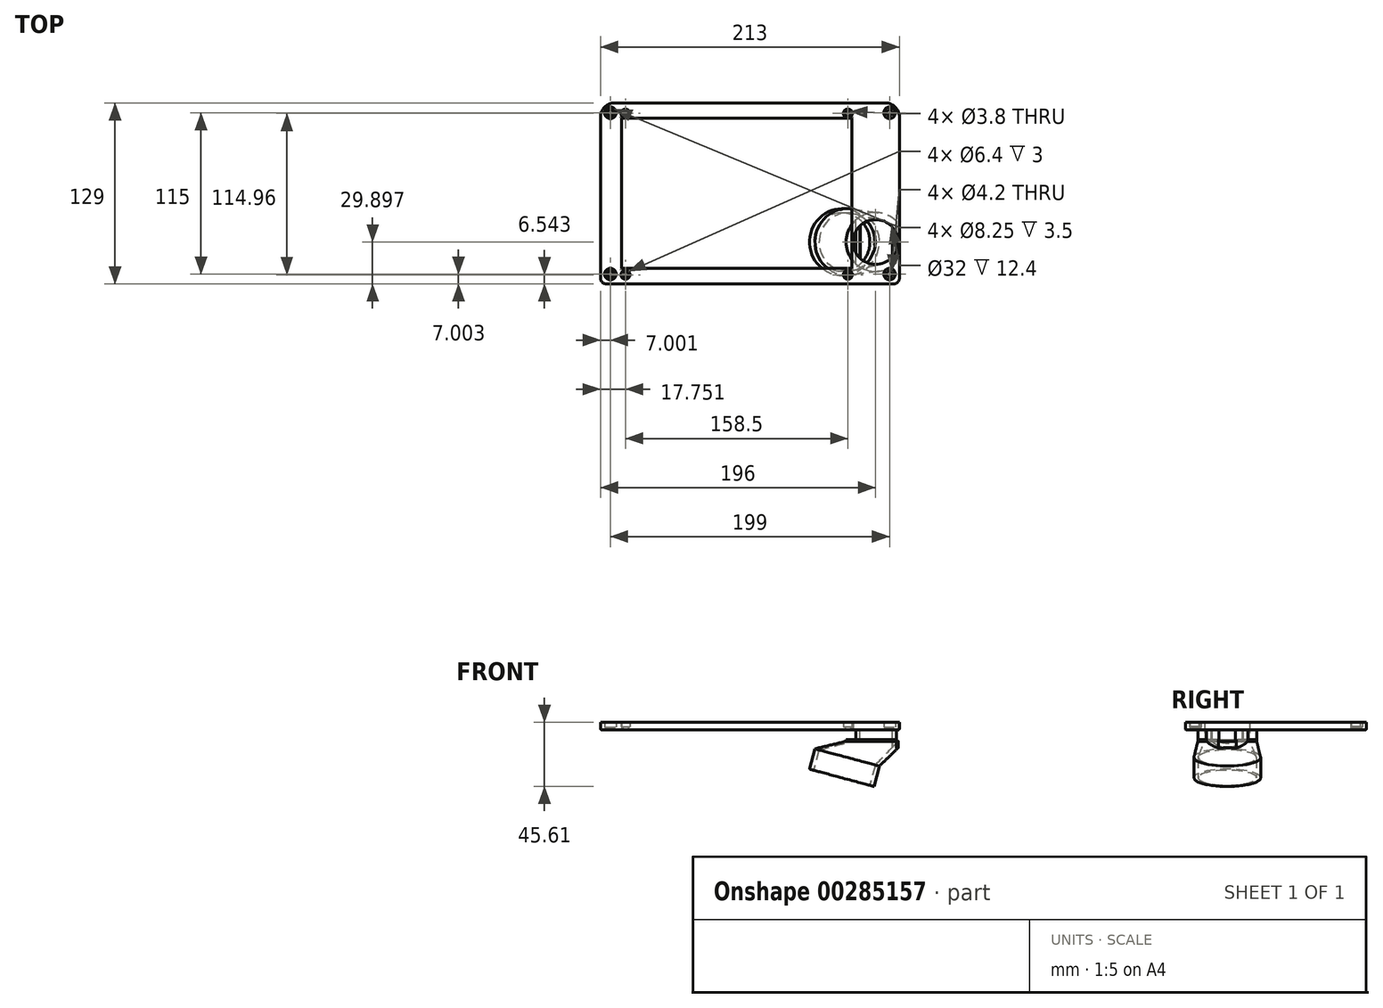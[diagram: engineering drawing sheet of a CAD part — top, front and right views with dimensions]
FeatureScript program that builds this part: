
annotation { "Feature Type Name" : "Feature", "Feature Type Description" : "" }
export const myFeature = defineFeature(function(context is Context, id is Id, definition is map)
    precondition{}
    {
        {
            var Q0;
            Q0=qCreatedBy(makeId("Top.planeOp"),FACE);
            var sketch = newSketch(context, id + "F0", { "sketchPlane" : qUnion([Q0])});
            skLineSegment(sketch, "E0.bottom", {"start": v(-110.3, 61) * mm, "end": v(82.7, 61) * mm});
            skLineSegment(sketch, "E0.top", {"start": v(-116.3, -68) * mm, "end": v(88.7, -68) * mm});
            skLineSegment(sketch, "E0.left", {"start": v(-120.3, 51) * mm, "end": v(-120.3, -64) * mm});
            skLineSegment(sketch, "E0.right", {"start": v(92.7, 51) * mm, "end": v(92.7, -64) * mm});
            skPoint(sketch, "E0.middle", {"position": v(-13.8, -3.5) * mm});
            skPoint(sketch, "E1.visualSharp", {"position": v(92.7, 61) * mm});
            skArc(sketch, "E1.filletArc", {"start": v(92.7, 51) * mm, "mid": v(89.76, 58.06) * mm, "end": v(82.7, 61) * mm});
            skPoint(sketch, "E2.visualSharp", {"position": v(-120.3, 61) * mm});
            skArc(sketch, "E2.filletArc", {"start": v(-110.3, 61) * mm, "mid": v(-117.38, 58.06) * mm, "end": v(-120.3, 51) * mm});
            skPoint(sketch, "E3.visualSharp", {"position": v(-120.3, -68) * mm});
            skArc(sketch, "E3.filletArc", {"start": v(-120.3, -64) * mm, "mid": v(-119.14, -66.84) * mm, "end": v(-116.3, -68) * mm});
            skPoint(sketch, "E4.visualSharp", {"position": v(92.7, -68) * mm});
            skArc(sketch, "E4.filletArc", {"start": v(88.7, -68) * mm, "mid": v(91.52, -66.84) * mm, "end": v(92.7, -64) * mm});
            skLineSegment(sketch, "E5", {"start": v(-23.3, -3.5) * mm, "end": v(-13.8, -3.5) * mm, "construction": true});
            skPoint(sketch, "E6", {"position": v(-23.3, -3.5) * mm});
            skLineSegment(sketch, "E7.bottom", {"start": v(-105.3, -57) * mm, "end": v(58.7, -57) * mm});
            skLineSegment(sketch, "E7.top", {"start": v(-105.3, 50) * mm, "end": v(58.7, 50) * mm});
            skLineSegment(sketch, "E7.left", {"start": v(-105.3, -57) * mm, "end": v(-105.3, 50) * mm});
            skLineSegment(sketch, "E7.right", {"start": v(58.7, -57) * mm, "end": v(58.7, 50) * mm});
            skLineSegment(sketch, "E8", {"start": v(92.7, 0) * mm, "end": v(58.7, 0) * mm, "construction": true});
            skLineSegment(sketch, "E9", {"start": v(75.7, 0) * mm, "end": v(75.7, 61) * mm, "construction": true});
            skLineSegment(sketch, "E10", {"start": v(75.7, 61) * mm, "end": v(75.7, -68) * mm, "construction": true});
            skCircle(sketch, "E11", {"center": v(75.7, -38.11) * mm, "radius": 16 * mm});
            skLineSegment(sketch, "E12", {"start": v(-23.3, -57) * mm, "end": v(-23.3, 61) * mm, "construction": true});
            skPoint(sketch, "E12.endSnap0", {"position": v(-23.3, 50) * mm});
            skLineSegment(sketch, "E13", {"start": v(-23.3, 61) * mm, "end": v(-23.3, -68) * mm, "construction": true});
            skLineSegment(sketch, "E14", {"start": v(-23.3, -3.5) * mm, "end": v(-101.76, -3.5) * mm, "construction": true});
            skLineSegment(sketch, "E15", {"start": v(-102.56, 50) * mm, "end": v(-102.56, 53.5) * mm, "construction": true});
            skLineSegment(sketch, "E16", {"start": v(-102.56, 53.5) * mm, "end": v(-102.56, -61.47) * mm, "construction": true});
            skLineSegment(sketch, "E17.MirrorCS", {"start": v(55.94, 53.5) * mm, "end": v(55.94, -61.47) * mm, "construction": true});
            skPoint(sketch, "E18", {"position": v(-102.56, 53.5) * mm});
            skPoint(sketch, "E19", {"position": v(55.94, 53.5) * mm});
            skPoint(sketch, "E20", {"position": v(55.94, -61.47) * mm});
            skPoint(sketch, "E21", {"position": v(-102.56, -61.47) * mm});
            skLineSegment(sketch, "E22", {"start": v(55.94, -61.47) * mm, "end": v(92.7, -61.47) * mm, "construction": true});
            skSolve(sketch);
        }
        {
            var Q0;
            Q0=makeQuery(id+"F0.imprint","IMPRINT",FACE,{"disambiguationData":[TD([[makeQuery(id+"F0.imprint","IMPRINT",EDGE,{"derivedFrom":sQuery(id+"F0.wireOp",EDGE,"E0.bottom")}),-1.0]])]});
            extrude(context, id + "F1", {"entities" : qUnion([Q0]), "depth" : 5.4 * mm});
        }
        {
            var Q0;
            Q0=makeQuery(id+"F1.opExtrude","CAP_FACE",FACE,{"disambiguationData":[OSD([sQuery(id+"F0.wireOp",EDGE,"E0.bottom"),sQuery(id+"F0.wireOp",EDGE,"E0.top"),sQuery(id+"F0.wireOp",EDGE,"E0.left"),sQuery(id+"F0.wireOp",EDGE,"E0.right"),sQuery(id+"F0.wireOp",EDGE,"E1.filletArc"),sQuery(id+"F0.wireOp",EDGE,"E2.filletArc"),sQuery(id+"F0.wireOp",EDGE,"E3.filletArc"),sQuery(id+"F0.wireOp",EDGE,"E4.filletArc"),sQuery(id+"F0.wireOp",EDGE,"E7.bottom"),sQuery(id+"F0.wireOp",EDGE,"E7.top"),sQuery(id+"F0.wireOp",EDGE,"E7.left"),sQuery(id+"F0.wireOp",EDGE,"E7.right"),sQuery(id+"F0.wireOp",EDGE,"E11")])],"isStart":true});
            var sketch = newSketch(context, id + "F2", { "sketchPlane" : qUnion([Q0])});
            skPoint(sketch, "E23.0", {"position": v(-102.56, 61.47) * mm});
            skPoint(sketch, "E24.0", {"position": v(55.94, 61.47) * mm});
            skPoint(sketch, "E25.0", {"position": v(-102.56, -53.5) * mm});
            skPoint(sketch, "E26.0", {"position": v(55.94, -53.5) * mm});
            skCircle(sketch, "E27", {"center": v(75.7, 38.11) * mm, "radius": 21 * mm});
            skCircle(sketch, "E28", {"center": v(75.7, 38.11) * mm, "radius": 24.25 * mm});
            skLineSegment(sketch, "E29.0", {"start": v(58.7, 57) * mm, "end": v(58.7, -50) * mm});
            skLineSegment(sketch, "E30.0", {"start": v(92.7, -51) * mm, "end": v(92.7, 64) * mm});
            skSolve(sketch);
        }
        {
            var Q0;
            Q0=makeQuery(id+"F1.opExtrude","CAP_FACE",FACE,{"disambiguationData":[OSD([sQuery(id+"F0.wireOp",EDGE,"E0.bottom"),sQuery(id+"F0.wireOp",EDGE,"E0.top"),sQuery(id+"F0.wireOp",EDGE,"E0.left"),sQuery(id+"F0.wireOp",EDGE,"E0.right"),sQuery(id+"F0.wireOp",EDGE,"E1.filletArc"),sQuery(id+"F0.wireOp",EDGE,"E2.filletArc"),sQuery(id+"F0.wireOp",EDGE,"E3.filletArc"),sQuery(id+"F0.wireOp",EDGE,"E4.filletArc"),sQuery(id+"F0.wireOp",EDGE,"E7.bottom"),sQuery(id+"F0.wireOp",EDGE,"E7.top"),sQuery(id+"F0.wireOp",EDGE,"E7.left"),sQuery(id+"F0.wireOp",EDGE,"E7.right"),sQuery(id+"F0.wireOp",EDGE,"E11")])],"isStart":false});
            var sketch = newSketch(context, id + "F3", { "sketchPlane" : qUnion([Q0])});
            skPoint(sketch, "E31.0", {"position": v(-102.56, 53.5) * mm});
            skPoint(sketch, "E32.0", {"position": v(55.94, 53.5) * mm});
            skPoint(sketch, "E33.0", {"position": v(55.94, -61.47) * mm});
            skPoint(sketch, "E34.0", {"position": v(-102.56, -61.47) * mm});
            skArc(sketch, "E35.0.0", {"start": v(-120.3, -64) * mm, "mid": v(-119.14, -66.84) * mm, "end": v(-116.3, -68) * mm});
            skLineSegment(sketch, "E35.0.1", {"start": v(-116.3, -68) * mm, "end": v(88.7, -68) * mm});
            skArc(sketch, "E35.0.2", {"start": v(88.7, -68) * mm, "mid": v(91.52, -66.84) * mm, "end": v(92.7, -64) * mm});
            skLineSegment(sketch, "E35.0.3", {"start": v(92.7, -64) * mm, "end": v(92.7, 51) * mm});
            skArc(sketch, "E35.0.4", {"start": v(92.7, 51) * mm, "mid": v(89.76, 58.06) * mm, "end": v(82.7, 61) * mm});
            skLineSegment(sketch, "E35.0.5", {"start": v(82.7, 61) * mm, "end": v(-110.3, 61) * mm});
            skArc(sketch, "E35.0.6", {"start": v(-110.3, 61) * mm, "mid": v(-117.38, 58.06) * mm, "end": v(-120.3, 51) * mm});
            skLineSegment(sketch, "E35.0.7", {"start": v(-120.3, 51) * mm, "end": v(-120.3, -64) * mm});
            skLineSegment(sketch, "E36", {"start": v(92.7, -61) * mm, "end": v(85.7, -61) * mm, "construction": true});
            skLineSegment(sketch, "E37", {"start": v(85.7, -61) * mm, "end": v(85.7, -68) * mm, "construction": true});
            skLineSegment(sketch, "E38", {"start": v(-113.3, -68) * mm, "end": v(-113.3, -61) * mm, "construction": true});
            skLineSegment(sketch, "E39", {"start": v(-113.3, -61) * mm, "end": v(-120.3, -61) * mm, "construction": true});
            skPoint(sketch, "E40", {"position": v(85.7, -61) * mm});
            skPoint(sketch, "E41", {"position": v(-113.3, -61) * mm});
            skLineSegment(sketch, "E42", {"start": v(85.7, 61) * mm, "end": v(85.7, 54) * mm, "construction": true});
            skLineSegment(sketch, "E43", {"start": v(-113.3, 61) * mm, "end": v(-113.3, 54) * mm, "construction": true});
            skLineSegment(sketch, "E44", {"start": v(-110.3, 61) * mm, "end": v(-125.94, 61) * mm, "construction": true});
            skLineSegment(sketch, "E45", {"start": v(-120.3, 51) * mm, "end": v(-120.3, 61) * mm, "construction": true});
            skLineSegment(sketch, "E46", {"start": v(-120.3, 54) * mm, "end": v(-113.3, 54) * mm, "construction": true});
            skLineSegment(sketch, "E47", {"start": v(82.7, 61) * mm, "end": v(120.1, 61) * mm, "construction": true});
            skLineSegment(sketch, "E48", {"start": v(92.7, 51) * mm, "end": v(92.7, 61) * mm, "construction": true});
            skLineSegment(sketch, "E49", {"start": v(92.7, 54) * mm, "end": v(85.7, 54) * mm, "construction": true});
            skPoint(sketch, "E50", {"position": v(-113.3, 54) * mm});
            skPoint(sketch, "E51", {"position": v(85.7, 54) * mm});
            skLineSegment(sketch, "E52", {"start": v(-113.3, 54) * mm, "end": v(-117.38, 58.06) * mm, "construction": true});
            skLineSegment(sketch, "E53", {"start": v(-119.14, -66.84) * mm, "end": v(-113.3, -61) * mm});
            skSolve(sketch);
        }
        {
            var Q0;
            Q0=sQuery(id+"F3.wireOp",VERTEX,"E34.0");
            var Q1;
            Q1=sQuery(id+"F3.wireOp",VERTEX,"E33.0");
            var Q2;
            Q2=sQuery(id+"F3.wireOp",VERTEX,"E32.0");
            var Q3;
            Q3=sQuery(id+"F3.wireOp",VERTEX,"E31.0");
            var Q4;
            Q4=makeQuery(id+"F1.opExtrude","SWEPT_BODY",BODY,{"disambiguationData":[OSD([sQuery(id+"F0.wireOp",EDGE,"E0.bottom"),sQuery(id+"F0.wireOp",EDGE,"E0.top"),sQuery(id+"F0.wireOp",EDGE,"E0.left"),sQuery(id+"F0.wireOp",EDGE,"E0.right"),sQuery(id+"F0.wireOp",EDGE,"E1.filletArc"),sQuery(id+"F0.wireOp",EDGE,"E2.filletArc"),sQuery(id+"F0.wireOp",EDGE,"E3.filletArc"),sQuery(id+"F0.wireOp",EDGE,"E4.filletArc"),sQuery(id+"F0.wireOp",EDGE,"E7.bottom"),sQuery(id+"F0.wireOp",EDGE,"E7.top"),sQuery(id+"F0.wireOp",EDGE,"E7.left"),sQuery(id+"F0.wireOp",EDGE,"E7.right"),sQuery(id+"F0.wireOp",EDGE,"E11")])]});
            hole(context, id + "F4", {"style" : HoleStyle.C_BORE, "endStyle" : HoleEndStyle.THROUGH, "holeDiameter" : 3.8 * mm, "cBoreDiameter" : 6.4 * mm, "cBoreDepth" : 3 * mm, "tappedDepth" : 12 * mm, "tapClearance" : 3, "locations" : qUnion([Q0, Q1, Q2, Q3]), "scope" : qUnion([Q4]), "startStyle" : HoleStartStyle.PART});
        }
        {
            var Q0;
            Q0=sQuery(id+"F3.wireOp",VERTEX,"E41");
            var Q1;
            Q1=sQuery(id+"F3.wireOp",VERTEX,"E50");
            var Q2;
            Q2=sQuery(id+"F3.wireOp",VERTEX,"E51");
            var Q3;
            Q3=sQuery(id+"F3.wireOp",VERTEX,"E40");
            var Q4;
            Q4=makeQuery(id+"F1.opExtrude","SWEPT_BODY",BODY,{"disambiguationData":[OSD([sQuery(id+"F0.wireOp",EDGE,"E0.bottom"),sQuery(id+"F0.wireOp",EDGE,"E0.top"),sQuery(id+"F0.wireOp",EDGE,"E0.left"),sQuery(id+"F0.wireOp",EDGE,"E0.right"),sQuery(id+"F0.wireOp",EDGE,"E1.filletArc"),sQuery(id+"F0.wireOp",EDGE,"E2.filletArc"),sQuery(id+"F0.wireOp",EDGE,"E3.filletArc"),sQuery(id+"F0.wireOp",EDGE,"E4.filletArc"),sQuery(id+"F0.wireOp",EDGE,"E7.bottom"),sQuery(id+"F0.wireOp",EDGE,"E7.top"),sQuery(id+"F0.wireOp",EDGE,"E7.left"),sQuery(id+"F0.wireOp",EDGE,"E7.right"),sQuery(id+"F0.wireOp",EDGE,"E11")])]});
            hole(context, id + "F5", {"style" : HoleStyle.C_BORE, "endStyle" : HoleEndStyle.THROUGH, "holeDiameter" : 4.2 * mm, "cBoreDiameter" : 8.25 * mm, "cBoreDepth" : 3.5 * mm, "tappedDepth" : 12 * mm, "tapClearance" : 3, "locations" : qUnion([Q0, Q1, Q2, Q3]), "scope" : qUnion([Q4]), "startStyle" : HoleStartStyle.PART});
        }
        {
            var Q0;
            {var subQ0=sQuery(id+"F0.wireOp",EDGE,"E7.right");var subQ1=sQuery(id+"F0.wireOp",EDGE,"E0.right");var subQ2=sQuery(id+"F2.wireOp",EDGE,"E28");Q0=makeQuery(id+"FXzu7cfs2hGkWBK_1.boolean.opBoolean","COPY",EDGE,{"disambiguationData":[TD([makeQuery(id+"F1.opExtrude","CAP_FACE",FACE,{"disambiguationData":[OSD([sQuery(id+"F0.wireOp",EDGE,"E0.bottom"),sQuery(id+"F0.wireOp",EDGE,"E0.top"),sQuery(id+"F0.wireOp",EDGE,"E0.left"),subQ1,sQuery(id+"F0.wireOp",EDGE,"E1.filletArc"),sQuery(id+"F0.wireOp",EDGE,"E2.filletArc"),sQuery(id+"F0.wireOp",EDGE,"E3.filletArc"),sQuery(id+"F0.wireOp",EDGE,"E4.filletArc"),sQuery(id+"F0.wireOp",EDGE,"E7.bottom"),sQuery(id+"F0.wireOp",EDGE,"E7.top"),sQuery(id+"F0.wireOp",EDGE,"E7.left"),subQ0,sQuery(id+"F0.wireOp",EDGE,"E11")])],"isStart":true}),makeQuery(id+"F1.opExtrude","SWEPT_FACE",FACE,{"disambiguationData":[OSD([subQ1])]}),makeQuery(id+"F1.opExtrude","SWEPT_FACE",FACE,{"disambiguationData":[OSD([subQ0])]}),makeQuery(id+"FXzu7cfs2hGkWBK_1.opExtrude","SWEPT_FACE",FACE,{"disambiguationData":[OSD([subQ2])]})])],"derivedFrom":makeQuery(id+"FXzu7cfs2hGkWBK_1.opExtrude","CAP_EDGE",EDGE,{"disambiguationData":[OSD([subQ2])],"isStart":true})});}
            var Q1;
            {var subQ0=sQuery(id+"F0.wireOp",EDGE,"E7.right");var subQ1=sQuery(id+"F2.wireOp",EDGE,"E28");Q1=makeQuery(id+"FXzu7cfs2hGkWBK_1.boolean.opBoolean","COPY",EDGE,{"disambiguationData":[TD([makeQuery(id+"F1.opExtrude","CAP_FACE",FACE,{"disambiguationData":[OSD([sQuery(id+"F0.wireOp",EDGE,"E0.bottom"),sQuery(id+"F0.wireOp",EDGE,"E0.top"),sQuery(id+"F0.wireOp",EDGE,"E0.left"),sQuery(id+"F0.wireOp",EDGE,"E0.right"),sQuery(id+"F0.wireOp",EDGE,"E1.filletArc"),sQuery(id+"F0.wireOp",EDGE,"E2.filletArc"),sQuery(id+"F0.wireOp",EDGE,"E3.filletArc"),sQuery(id+"F0.wireOp",EDGE,"E4.filletArc"),sQuery(id+"F0.wireOp",EDGE,"E7.bottom"),sQuery(id+"F0.wireOp",EDGE,"E7.top"),sQuery(id+"F0.wireOp",EDGE,"E7.left"),subQ0,sQuery(id+"F0.wireOp",EDGE,"E11")])],"isStart":true}),makeQuery(id+"F1.opExtrude","SWEPT_FACE",FACE,{"disambiguationData":[OSD([subQ0])]}),makeQuery(id+"F5.hole-3.boolean.opBoolean","COPY",FACE,{"derivedFrom":makeQuery(id+"F5.hole-3.opRevolve","SWEPT_FACE",FACE,{"disambiguationData":[OSD([sQuery(id+"F5.hole-3.sketch.wireOp",EDGE,"core_line_2")])]})}),makeQuery(id+"FXzu7cfs2hGkWBK_1.opExtrude","SWEPT_FACE",FACE,{"disambiguationData":[OSD([subQ1])]})])],"derivedFrom":makeQuery(id+"FXzu7cfs2hGkWBK_1.opExtrude","CAP_EDGE",EDGE,{"disambiguationData":[OSD([subQ1])],"isStart":true})});}
            var Q2;
            Q2=makeQuery(id+"F1.opExtrude","CAP_EDGE",EDGE,{"disambiguationData":[OSD([sQuery(id+"F0.wireOp",EDGE,"E0.left")])],"isStart":true});
            var Q3;
            Q3=makeQuery(id+"F1.opExtrude","CAP_EDGE",EDGE,{"disambiguationData":[OSD([sQuery(id+"F0.wireOp",EDGE,"E2.filletArc")])],"isStart":true});
            var Q4;
            Q4=makeQuery(id+"F1.opExtrude","CAP_EDGE",EDGE,{"disambiguationData":[OSD([sQuery(id+"F0.wireOp",EDGE,"E7.bottom")])],"isStart":true});
            var Q5;
            Q5=makeQuery(id+"F1.opExtrude","CAP_EDGE",EDGE,{"disambiguationData":[OSD([sQuery(id+"F0.wireOp",EDGE,"E7.left")])],"isStart":true});
            var Q6;
            Q6=makeQuery(id+"F1.opExtrude","CAP_EDGE",EDGE,{"disambiguationData":[OSD([sQuery(id+"F0.wireOp",EDGE,"E7.top")])],"isStart":true});
            var Q7;
            {var subQ0=sQuery(id+"F0.wireOp",EDGE,"E7.right");var subQ1=sQuery(id+"F0.wireOp",EDGE,"E7.bottom");Q7=makeQuery(id+"FXzu7cfs2hGkWBK_1.boolean.opBoolean","SPLIT",EDGE,{"disambiguationData":[TD([makeQuery(id+"F1.opExtrude","SWEPT_FACE",FACE,{"disambiguationData":[OSD([subQ1])]})])],"derivedFrom":makeQuery(id+"F1.opExtrude","CAP_EDGE",EDGE,{"disambiguationData":[OSD([subQ0])],"isStart":true})});}
            var Q8;
            {var subQ0=sQuery(id+"F0.wireOp",EDGE,"E7.right");Q8=makeQuery(id+"FXzu7cfs2hGkWBK_1.boolean.opBoolean","SPLIT",EDGE,{"disambiguationData":[TD([makeQuery(id+"FXzu7cfs2hGkWBK_1.opExtrude","SWEPT_FACE",FACE,{"disambiguationData":[OSD([sQuery(id+"F2.wireOp",EDGE,"E27")])]})])],"derivedFrom":makeQuery(id+"F1.opExtrude","CAP_EDGE",EDGE,{"disambiguationData":[OSD([subQ0])],"isStart":true})});}
            var Q9;
            {var subQ0=sQuery(id+"F0.wireOp",EDGE,"E7.right");var subQ1=sQuery(id+"F0.wireOp",EDGE,"E7.top");var subQ3=makeQuery(id+"F1.opExtrude","SWEPT_FACE",FACE,{"disambiguationData":[OSD([subQ1])]});Q9=makeQuery(id+"FAuTDVlshv62hnW_1.boolean.opBoolean","SPLIT",EDGE,{"disambiguationData":[TD([subQ3])],"derivedFrom":makeQuery(id+"FXzu7cfs2hGkWBK_1.boolean.opBoolean","SPLIT",EDGE,{"disambiguationData":[TD([subQ3])],"derivedFrom":makeQuery(id+"F1.opExtrude","CAP_EDGE",EDGE,{"disambiguationData":[OSD([subQ0])],"isStart":true})})});}
            var Q10;
            {var subQ0=sQuery(id+"F0.wireOp",EDGE,"E7.right");var subQ1=sQuery(id+"F0.wireOp",EDGE,"E7.top");var subQ2=sQuery(id+"F0.wireOp",EDGE,"E0.right");var subQ3=makeQuery(id+"F1.opExtrude","CAP_FACE",FACE,{"disambiguationData":[OSD([sQuery(id+"F0.wireOp",EDGE,"E0.bottom"),sQuery(id+"F0.wireOp",EDGE,"E0.top"),sQuery(id+"F0.wireOp",EDGE,"E0.left"),subQ2,sQuery(id+"F0.wireOp",EDGE,"E1.filletArc"),sQuery(id+"F0.wireOp",EDGE,"E2.filletArc"),sQuery(id+"F0.wireOp",EDGE,"E3.filletArc"),sQuery(id+"F0.wireOp",EDGE,"E4.filletArc"),sQuery(id+"F0.wireOp",EDGE,"E7.bottom"),subQ1,sQuery(id+"F0.wireOp",EDGE,"E7.left"),subQ0,sQuery(id+"F0.wireOp",EDGE,"E11")])],"isStart":true});var subQ4=makeQuery(id+"F1.opExtrude","SWEPT_FACE",FACE,{"disambiguationData":[OSD([subQ0])]});var subQ5=sQuery(id+"F2.wireOp",EDGE,"E28");var subQ6=makeQuery(id+"FXzu7cfs2hGkWBK_1.opExtrude","SWEPT_FACE",FACE,{"disambiguationData":[OSD([subQ5])]});Q10=makeQuery(id+"FAuTDVlshv62hnW_1.boolean.opBoolean","SPLIT",EDGE,{"disambiguationData":[TD([makeQuery(id+"FXzu7cfs2hGkWBK_1.boolean.opBoolean","COPY",FACE,{"disambiguationData":[TD([subQ3,makeQuery(id+"F1.opExtrude","SWEPT_FACE",FACE,{"disambiguationData":[OSD([subQ2])]}),subQ4,makeQuery(id+"FXzu7cfs2hGkWBK_1.opExtrude","CAP_FACE",FACE,{"disambiguationData":[OSD([sQuery(id+"F2.wireOp",EDGE,"E27"),subQ5])],"isStart":false})])],"derivedFrom":subQ6})])],"derivedFrom":makeQuery(id+"FXzu7cfs2hGkWBK_1.boolean.opBoolean","SPLIT",EDGE,{"disambiguationData":[TD([makeQuery(id+"F1.opExtrude","SWEPT_FACE",FACE,{"disambiguationData":[OSD([subQ1])]})])],"derivedFrom":makeQuery(id+"F1.opExtrude","CAP_EDGE",EDGE,{"disambiguationData":[OSD([subQ0])],"isStart":true})})});}
            var Q11;
            {var subQ0=sQuery(id+"F0.wireOp",EDGE,"E7.right");var subQ1=sQuery(id+"F0.wireOp",EDGE,"E7.top");Q11=makeQuery(id+"FAuTDVlshv62hnW_1.boolean.opBoolean","SPLIT",EDGE,{"disambiguationData":[TD([makeQuery(id+"FAuTDVlshv62hnW_1.opExtrude","SWEPT_FACE",FACE,{"disambiguationData":[OSD([sQuery(id+"F2.wireOp",EDGE,"AH5NIqyg-kwf5-ivtZ-E1gb-oLSIGUMr4FpD")])]})])],"derivedFrom":makeQuery(id+"FXzu7cfs2hGkWBK_1.boolean.opBoolean","SPLIT",EDGE,{"disambiguationData":[TD([makeQuery(id+"F1.opExtrude","SWEPT_FACE",FACE,{"disambiguationData":[OSD([subQ1])]})])],"derivedFrom":makeQuery(id+"F1.opExtrude","CAP_EDGE",EDGE,{"disambiguationData":[OSD([subQ0])],"isStart":true})})});}
            var Q12;
            Q12=makeQuery(id+"FAuTDVlshv62hnW_1.boolean.opBoolean","COPY",EDGE,{"disambiguationData":[OD(0.0)],"derivedFrom":makeQuery(id+"FAuTDVlshv62hnW_1.opExtrude","CAP_EDGE",EDGE,{"disambiguationData":[OSD([sQuery(id+"F2.wireOp",EDGE,"opVQtyLN-j1gY-ZvLt-gBJu-Jvu7VNzgkRLF")])],"isStart":true})});
            var Q13;
            Q13=makeQuery(id+"FAuTDVlshv62hnW_1.boolean.opBoolean","COPY",EDGE,{"disambiguationData":[OD(1.0)],"derivedFrom":makeQuery(id+"FAuTDVlshv62hnW_1.opExtrude","CAP_EDGE",EDGE,{"disambiguationData":[OSD([sQuery(id+"F2.wireOp",EDGE,"opVQtyLN-j1gY-ZvLt-gBJu-Jvu7VNzgkRLF")])],"isStart":true})});
            var Q14;
            Q14=makeQuery(id+"F1.opExtrude","CAP_EDGE",EDGE,{"disambiguationData":[OSD([sQuery(id+"F0.wireOp",EDGE,"E0.bottom")])],"isStart":true});
            var Q15;
            Q15=makeQuery(id+"F1.opExtrude","CAP_EDGE",EDGE,{"disambiguationData":[OSD([sQuery(id+"F0.wireOp",EDGE,"E1.filletArc")])],"isStart":true});
            var Q16;
            {var subQ0=sQuery(id+"F0.wireOp",EDGE,"E0.right");Q16=makeQuery(id+"FXzu7cfs2hGkWBK_1.boolean.opBoolean","SPLIT",EDGE,{"disambiguationData":[TD([makeQuery(id+"FXzu7cfs2hGkWBK_1.opExtrude","SWEPT_FACE",FACE,{"disambiguationData":[OSD([sQuery(id+"F2.wireOp",EDGE,"E27")])]})])],"derivedFrom":makeQuery(id+"F1.opExtrude","CAP_EDGE",EDGE,{"disambiguationData":[OSD([subQ0])],"isStart":true})});}
            var Q17;
            {var subQ0=sQuery(id+"F0.wireOp",EDGE,"E1.filletArc");var subQ1=sQuery(id+"F0.wireOp",EDGE,"E0.right");var subQ3=makeQuery(id+"F1.opExtrude","SWEPT_FACE",FACE,{"disambiguationData":[OSD([subQ0])]});Q17=makeQuery(id+"FAuTDVlshv62hnW_1.boolean.opBoolean","SPLIT",EDGE,{"disambiguationData":[TD([subQ3])],"derivedFrom":makeQuery(id+"FXzu7cfs2hGkWBK_1.boolean.opBoolean","SPLIT",EDGE,{"disambiguationData":[TD([subQ3])],"derivedFrom":makeQuery(id+"F1.opExtrude","CAP_EDGE",EDGE,{"disambiguationData":[OSD([subQ1])],"isStart":true})})});}
            var Q18;
            {var subQ0=sQuery(id+"F0.wireOp",EDGE,"E7.right");var subQ1=sQuery(id+"F0.wireOp",EDGE,"E1.filletArc");var subQ2=sQuery(id+"F0.wireOp",EDGE,"E0.right");var subQ3=makeQuery(id+"F1.opExtrude","CAP_FACE",FACE,{"disambiguationData":[OSD([sQuery(id+"F0.wireOp",EDGE,"E0.bottom"),sQuery(id+"F0.wireOp",EDGE,"E0.top"),sQuery(id+"F0.wireOp",EDGE,"E0.left"),subQ2,subQ1,sQuery(id+"F0.wireOp",EDGE,"E2.filletArc"),sQuery(id+"F0.wireOp",EDGE,"E3.filletArc"),sQuery(id+"F0.wireOp",EDGE,"E4.filletArc"),sQuery(id+"F0.wireOp",EDGE,"E7.bottom"),sQuery(id+"F0.wireOp",EDGE,"E7.top"),sQuery(id+"F0.wireOp",EDGE,"E7.left"),subQ0,sQuery(id+"F0.wireOp",EDGE,"E11")])],"isStart":true});var subQ4=makeQuery(id+"F1.opExtrude","SWEPT_FACE",FACE,{"disambiguationData":[OSD([subQ2])]});var subQ5=sQuery(id+"F2.wireOp",EDGE,"E28");var subQ6=makeQuery(id+"FXzu7cfs2hGkWBK_1.opExtrude","SWEPT_FACE",FACE,{"disambiguationData":[OSD([subQ5])]});Q18=makeQuery(id+"FAuTDVlshv62hnW_1.boolean.opBoolean","SPLIT",EDGE,{"disambiguationData":[TD([makeQuery(id+"FXzu7cfs2hGkWBK_1.boolean.opBoolean","COPY",FACE,{"disambiguationData":[TD([subQ3,subQ4,makeQuery(id+"F1.opExtrude","SWEPT_FACE",FACE,{"disambiguationData":[OSD([subQ0])]}),makeQuery(id+"FXzu7cfs2hGkWBK_1.opExtrude","CAP_FACE",FACE,{"disambiguationData":[OSD([sQuery(id+"F2.wireOp",EDGE,"E27"),subQ5])],"isStart":false})])],"derivedFrom":subQ6})])],"derivedFrom":makeQuery(id+"FXzu7cfs2hGkWBK_1.boolean.opBoolean","SPLIT",EDGE,{"disambiguationData":[TD([makeQuery(id+"F1.opExtrude","SWEPT_FACE",FACE,{"disambiguationData":[OSD([subQ1])]})])],"derivedFrom":makeQuery(id+"F1.opExtrude","CAP_EDGE",EDGE,{"disambiguationData":[OSD([subQ2])],"isStart":true})})});}
            var Q19;
            {var subQ0=sQuery(id+"F0.wireOp",EDGE,"E1.filletArc");var subQ1=sQuery(id+"F0.wireOp",EDGE,"E0.right");Q19=makeQuery(id+"FAuTDVlshv62hnW_1.boolean.opBoolean","SPLIT",EDGE,{"disambiguationData":[TD([makeQuery(id+"FAuTDVlshv62hnW_1.opExtrude","SWEPT_FACE",FACE,{"disambiguationData":[OSD([sQuery(id+"F2.wireOp",EDGE,"AH5NIqyg-kwf5-ivtZ-E1gb-oLSIGUMr4FpD")])]})])],"derivedFrom":makeQuery(id+"FXzu7cfs2hGkWBK_1.boolean.opBoolean","SPLIT",EDGE,{"disambiguationData":[TD([makeQuery(id+"F1.opExtrude","SWEPT_FACE",FACE,{"disambiguationData":[OSD([subQ0])]})])],"derivedFrom":makeQuery(id+"F1.opExtrude","CAP_EDGE",EDGE,{"disambiguationData":[OSD([subQ1])],"isStart":true})})});}
            var Q20;
            Q20=makeQuery(id+"F1.opExtrude","CAP_EDGE",EDGE,{"disambiguationData":[OSD([sQuery(id+"F0.wireOp",EDGE,"E4.filletArc")])],"isStart":true});
            var Q21;
            Q21=makeQuery(id+"F1.opExtrude","CAP_EDGE",EDGE,{"disambiguationData":[OSD([sQuery(id+"F0.wireOp",EDGE,"E3.filletArc")])],"isStart":true});
            var Q22;
            Q22=makeQuery(id+"FAuTDVlshv62hnW_1.boolean.opBoolean","COPY",EDGE,{"disambiguationData":[OD(0.0)],"derivedFrom":makeQuery(id+"FAuTDVlshv62hnW_1.opExtrude","CAP_EDGE",EDGE,{"disambiguationData":[OSD([sQuery(id+"F2.wireOp",EDGE,"AH5NIqyg-kwf5-ivtZ-E1gb-oLSIGUMr4FpD")])],"isStart":true})});
            var Q23;
            Q23=makeQuery(id+"FAuTDVlshv62hnW_1.boolean.opBoolean","COPY",EDGE,{"disambiguationData":[OD(1.0)],"derivedFrom":makeQuery(id+"FAuTDVlshv62hnW_1.opExtrude","CAP_EDGE",EDGE,{"disambiguationData":[OSD([sQuery(id+"F2.wireOp",EDGE,"AH5NIqyg-kwf5-ivtZ-E1gb-oLSIGUMr4FpD")])],"isStart":true})});
            var Q24;
            Q24=makeQuery(id+"FXzu7cfs2hGkWBK_1.boolean.opBoolean","COPY",EDGE,{"disambiguationData":[OD(0.0)],"derivedFrom":makeQuery(id+"FXzu7cfs2hGkWBK_1.opExtrude","CAP_EDGE",EDGE,{"disambiguationData":[OSD([sQuery(id+"F2.wireOp",EDGE,"E27")])],"isStart":true})});
            var Q25;
            Q25=makeQuery(id+"FXzu7cfs2hGkWBK_1.boolean.opBoolean","COPY",EDGE,{"disambiguationData":[OD(1.0)],"derivedFrom":makeQuery(id+"FXzu7cfs2hGkWBK_1.opExtrude","CAP_EDGE",EDGE,{"disambiguationData":[OSD([sQuery(id+"F2.wireOp",EDGE,"E27")])],"isStart":true})});
            var Q26;
            Q26=makeQuery(id+"F1.opExtrude","CAP_EDGE",EDGE,{"disambiguationData":[OSD([sQuery(id+"F0.wireOp",EDGE,"E0.top")])],"isStart":true});
            fillet(context, id + "F6", {"entities" : qUnion([Q0, Q1, Q2, Q3, Q4, Q5, Q6, Q7, Q8, Q9, Q10, Q11, Q12, Q13, Q14, Q15, Q16, Q17, Q18, Q19, Q20, Q21, Q22, Q23, Q24, Q25, Q26]), "radius" : 1 * mm, "tangentPropagation" : true, "allowEdgeOverflow" : false});
        }
        {
            var Q0;
            Q0=makeQuery(id+"F2.imprint","IMPRINT",FACE,{"disambiguationData":[TD([[makeQuery(id+"F2.imprint","IMPRINT",EDGE,{"derivedFrom":makeQuery(id+"F1.opExtrude","CAP_EDGE",EDGE,{"disambiguationData":[OSD([sQuery(id+"F0.wireOp",EDGE,"E11")])],"isStart":true})}),1.0]])]});
            var sketch = newSketch(context, id + "F7", { "sketchPlane" : qUnion([Q0])});
            skCircle(sketch, "E54.0", {"center": v(75.7, 38.11) * mm, "radius": 16 * mm});
            skCircle(sketch, "E55.0", {"center": v(75.7, 38.11) * mm, "radius": 21 * mm});
            skLineSegment(sketch, "E56", {"start": v(61.54, 53.63) * mm, "end": v(61.54, 22.6) * mm});
            skLineSegment(sketch, "E57", {"start": v(90.57, 52.93) * mm, "end": v(90.57, 23.3) * mm});
            skSolve(sketch);
        }
        {
            var Q0;
            Q0=makeQuery(id+"F0.imprint","IMPRINT",FACE,{"disambiguationData":[TD([[makeQuery(id+"F0.imprint","IMPRINT",EDGE,{"derivedFrom":sQuery(id+"F0.wireOp",EDGE,"E11")}),1.0]])]});
            cPlane(context, id + "F8", {"entities" : qUnion([Q0]), "cplaneType" : CPlaneType.OFFSET, "offset" : 35 * mm, "oppositeDirection" : true, "width" : 150 * mm, "height" : 150 * mm});
        }
        {
            var Q0;
            Q0=qCreatedBy(id+"F8.planeOp",FACE);
            var sketch = newSketch(context, id + "F9", { "sketchPlane" : qUnion([Q0])});
            skPoint(sketch, "E58.0", {"position": v(75.7, -38.11) * mm});
            skLineSegment(sketch, "E59", {"start": v(75.7, -38.11) * mm, "end": v(60.7, -38.11) * mm, "construction": true});
            skCircle(sketch, "E60", {"center": v(60.7, -38.11) * mm, "radius": 20.75 * mm});
            skCircle(sketch, "E61", {"center": v(60.7, -38.11) * mm, "radius": 23.75 * mm});
            skSolve(sketch);
        }
        {
            var Q0;
            Q0=makeQuery(id+"F9.imprint","IMPRINT",FACE,{"disambiguationData":[TD([[makeQuery(id+"F9.imprint","IMPRINT",EDGE,{"derivedFrom":sQuery(id+"F9.wireOp",EDGE,"E60")}),-1.0]])]});
            extrude(context, id + "F10", {"entities" : qUnion([Q0]), "operationType" : NewBodyOperationType.ADD, "depth" : 15 * mm});
        }
        {
            var Q0;
            Q0=makeQuery(id+"F10.opExtrude","SWEPT_BODY",BODY,{"disambiguationData":[OSD([sQuery(id+"F9.wireOp",EDGE,"E60"),sQuery(id+"F9.wireOp",EDGE,"E61"),sQuery(id+"F9.wireOp",EDGE,"JfIrUzmG-d9lY-iVxp-Mb9g-9npJm7Iwwub6"),sQuery(id+"F9.wireOp",EDGE,"MjCc8q1w-3G2U-IAaR-hrDx-Pos9HdKJ4R0N")])]});
            var Q1;
            Q1=makeQuery(id+"F10.opExtrude","SWEPT_BODY",BODY,{"disambiguationData":[OSD([sQuery(id+"F9.wireOp",EDGE,"E60"),sQuery(id+"F9.wireOp",EDGE,"E61"),sQuery(id+"F9.wireOp",EDGE,"8tNqm4Kz-eikn-GZsH-ny9o-i7E9EC5gfrlz"),sQuery(id+"F9.wireOp",EDGE,"Jv5iIJlW-SeG2-jAlZ-grfs-9UxCIiy8JIfF")])]});
            var Q2;
            {var subQ0=sQuery(id+"F0.wireOp",EDGE,"E7.right");Q2=makeQuery(id+"F6.opFillet","BLEND_EDGE",EDGE,{"disambiguationData":[OD(0.0)],"blendedFrom":[makeQuery(id+"F1.opExtrude","CAP_EDGE",EDGE,{"disambiguationData":[OSD([subQ0])],"isStart":true}),makeQuery(id+"F1.opExtrude","CAP_FACE",FACE,{"disambiguationData":[OSD([sQuery(id+"F0.wireOp",EDGE,"E0.bottom"),sQuery(id+"F0.wireOp",EDGE,"E0.top"),sQuery(id+"F0.wireOp",EDGE,"E0.left"),sQuery(id+"F0.wireOp",EDGE,"E0.right"),sQuery(id+"F0.wireOp",EDGE,"E1.filletArc"),sQuery(id+"F0.wireOp",EDGE,"E2.filletArc"),sQuery(id+"F0.wireOp",EDGE,"E3.filletArc"),sQuery(id+"F0.wireOp",EDGE,"E4.filletArc"),sQuery(id+"F0.wireOp",EDGE,"E7.bottom"),sQuery(id+"F0.wireOp",EDGE,"E7.top"),sQuery(id+"F0.wireOp",EDGE,"E7.left"),subQ0,sQuery(id+"F0.wireOp",EDGE,"E11")])],"isStart":true})],"blendedInto":[makeQuery(id+"F1.opExtrude","CAP_FACE",FACE,{"disambiguationData":[OSD([sQuery(id+"F0.wireOp",EDGE,"E0.bottom"),sQuery(id+"F0.wireOp",EDGE,"E0.top"),sQuery(id+"F0.wireOp",EDGE,"E0.left"),sQuery(id+"F0.wireOp",EDGE,"E0.right"),sQuery(id+"F0.wireOp",EDGE,"E1.filletArc"),sQuery(id+"F0.wireOp",EDGE,"E2.filletArc"),sQuery(id+"F0.wireOp",EDGE,"E3.filletArc"),sQuery(id+"F0.wireOp",EDGE,"E4.filletArc"),sQuery(id+"F0.wireOp",EDGE,"E7.bottom"),sQuery(id+"F0.wireOp",EDGE,"E7.top"),sQuery(id+"F0.wireOp",EDGE,"E7.left"),subQ0,sQuery(id+"F0.wireOp",EDGE,"E11")])],"isStart":true})]});}
            transform(context, id + "F11", {"entities" : qUnion([Q0, Q1]), "transformType" : TransformType.ROTATION, "transformAxis" : qUnion([Q2]), "angle" : 15 * degree, "makeCopy" : false});
        }
        {
            var Q0;
            Q0=makeQuery(id+"F7.imprint","IMPRINT",FACE,{"disambiguationData":[TD([[makeQuery(id+"F7.imprint","IMPRINT",EDGE,{"derivedFrom":sQuery(id+"F7.wireOp",EDGE,"E54.0")}),1.0]])]});
            extrude(context, id + "F12", {"entities" : qUnion([Q0]), "depth" : 7 * mm});
        }
        {
            var Q0;
            {var subQ0=sQuery(id+"F7.wireOp",EDGE,"E57");var subQ1=sQuery(id+"F7.wireOp",EDGE,"E55.0");var subQ2=makeQuery(id+"F7.imprint","INTERSECT",VERTEX,{"disambiguationData":[OD(1.0)],"derivedFrom":[subQ1,subQ0]});var subQ3=sQuery(id+"F7.wireOp",EDGE,"E54.0");var subQ5=sQuery(id+"F7.wireOp",EDGE,"E56");var subQ6=makeQuery(id+"F7.imprint","INTERSECT",VERTEX,{"disambiguationData":[OD(1.0)],"derivedFrom":[subQ1,subQ5]});var subQ7=makeQuery(id+"F7.imprint","INTERSECT",VERTEX,{"disambiguationData":[OD(0.0)],"derivedFrom":[subQ3,subQ5]});Q0=makeQuery(id+"F12.opExtrude","CAP_FACE",FACE,{"disambiguationData":[OSD([subQ3,subQ1,subQ5,subQ0]),TDD([makeQuery(id+"F7.imprint","IMPRINT",EDGE,{"disambiguationData":[TD([[subQ7,1.0]])],"derivedFrom":subQ3}),makeQuery(id+"F7.imprint","IMPRINT",EDGE,{"disambiguationData":[TD([[subQ6,-1.0]])],"derivedFrom":subQ1}),makeQuery(id+"F7.imprint","IMPRINT",EDGE,{"disambiguationData":[TD([[subQ6,1.0]])],"derivedFrom":subQ5}),makeQuery(id+"F7.imprint","IMPRINT",EDGE,{"disambiguationData":[TD([[subQ2,1.0]])],"derivedFrom":subQ0})])],"isStart":false});}
            var sketch = newSketch(context, id + "F13", { "sketchPlane" : qUnion([Q0])});
            skCircle(sketch, "E62", {"center": v(75.7, 38.11) * mm, "radius": 16.15 * mm});
            skCircle(sketch, "E63", {"center": v(75.7, 38.11) * mm, "radius": 20.97 * mm});
            skSolve(sketch);
        }
        {
            var Q0;
            Q0 = qSketchRegion(id + "F13", true);
            extrude(context, id + "F14", {"entities" : qUnion([Q0]), "operationType" : NewBodyOperationType.ADD, "depth" : 1 * mm});
        }
        {
            var Q0;
            Q0=makeQuery(id+"F14.opExtrude","CAP_FACE",FACE,{"disambiguationData":[OSD([sQuery(id+"F13.wireOp",EDGE,"E62"),sQuery(id+"F13.wireOp",EDGE,"E63")])],"isStart":false});
            var sketch = newSketch(context, id + "F15", { "sketchPlane" : qUnion([Q0])});
            skCircle(sketch, "E64.0.0", {"center": v(75.7, 38.11) * mm, "radius": 20.97 * mm});
            skCircle(sketch, "E65.0", {"center": v(75.7, 38.11) * mm, "radius": 16.15 * mm});
            skLineSegment(sketch, "E66", {"start": v(76.03, 21.96) * mm, "end": v(76.03, 17.14) * mm});
            skLineSegment(sketch, "E67", {"start": v(74.9, 59.07) * mm, "end": v(74.9, 54.25) * mm});
            skLineSegment(sketch, "E68", {"start": v(64.9, 50.13) * mm, "end": v(64.9, 26.1) * mm});
            skSolve(sketch);
        }
        {
            var Q0;
            Q0=makeQuery(id+"F10.opExtrude","CAP_FACE",FACE,{"disambiguationData":[OSD([sQuery(id+"F9.wireOp",EDGE,"E60"),sQuery(id+"F9.wireOp",EDGE,"E61")])],"isStart":false});
            var sketch = newSketch(context, id + "F16", { "sketchPlane" : qUnion([Q0])});
            skCircle(sketch, "E69.0.0", {"center": v(58.66, -38.11) * mm, "radius": 23.75 * mm});
            skCircle(sketch, "E70.0", {"center": v(58.66, -38.11) * mm, "radius": 20.75 * mm});
            skLineSegment(sketch, "E71", {"start": v(56.56, -17.47) * mm, "end": v(56.56, -14.46) * mm});
            skLineSegment(sketch, "E72", {"start": v(55.73, -58.66) * mm, "end": v(55.73, -61.68) * mm});
            skSolve(sketch);
        }
        {
            var Q0;
            {var subQ0=sQuery(id+"F15.wireOp",EDGE,"E66");Q0=makeQuery(id+"F15.imprint","IMPRINT",FACE,{"disambiguationData":[TD([[makeQuery(id+"F15.imprint","IMPRINT",EDGE,{"derivedFrom":subQ0}),1.0]])]});}
            var Q1;
            {var subQ0=sQuery(id+"F16.wireOp",EDGE,"E71");Q1=makeQuery(id+"F16.imprint","IMPRINT",FACE,{"disambiguationData":[TD([[makeQuery(id+"F16.imprint","IMPRINT",EDGE,{"derivedFrom":subQ0}),-1.0]])]});}
            loft(context, id + "F17", {"sheetProfilesArray" : [{ "sheetProfileEntities" : qUnion([Q0]) }, { "sheetProfileEntities" : qUnion([Q1]) }]});
        }
        {
            var Q1;
            {var subQ0=sQuery(id+"F15.wireOp",EDGE,"E66");Q1=makeQuery(id+"F15.imprint","IMPRINT",FACE,{"disambiguationData":[TD([[makeQuery(id+"F15.imprint","IMPRINT",EDGE,{"derivedFrom":subQ0}),-1.0]])]});}
            var Q2;
            {var subQ0=sQuery(id+"F16.wireOp",EDGE,"E71");Q2=makeQuery(id+"F16.imprint","IMPRINT",FACE,{"disambiguationData":[TD([[makeQuery(id+"F16.imprint","IMPRINT",EDGE,{"derivedFrom":subQ0}),1.0]])]});}
            loft(context, id + "F18", {"operationType" : NewBodyOperationType.ADD, "sheetProfilesArray" : [{ "sheetProfileEntities" : qUnion([Q1]) }, { "sheetProfileEntities" : qUnion([Q2]) }]});
        }
        {
            var Q0;
            {var subQ0=sQuery(id+"F7.wireOp",EDGE,"E57");var subQ1=sQuery(id+"F7.wireOp",EDGE,"E55.0");var subQ2=makeQuery(id+"F7.imprint","INTERSECT",VERTEX,{"disambiguationData":[OD(1.0)],"derivedFrom":[subQ1,subQ0]});var subQ3=sQuery(id+"F7.wireOp",EDGE,"E54.0");var subQ5=sQuery(id+"F7.wireOp",EDGE,"E56");var subQ6=makeQuery(id+"F7.imprint","INTERSECT",VERTEX,{"disambiguationData":[OD(1.0)],"derivedFrom":[subQ1,subQ5]});var subQ7=makeQuery(id+"F7.imprint","INTERSECT",VERTEX,{"disambiguationData":[OD(0.0)],"derivedFrom":[subQ3,subQ5]});Q0=makeQuery(id+"F12.opExtrude","CAP_FACE",FACE,{"disambiguationData":[OSD([subQ3,subQ1,subQ5,subQ0]),TDD([makeQuery(id+"F7.imprint","IMPRINT",EDGE,{"disambiguationData":[TD([[subQ7,1.0]])],"derivedFrom":subQ3}),makeQuery(id+"F7.imprint","IMPRINT",EDGE,{"disambiguationData":[TD([[subQ6,-1.0]])],"derivedFrom":subQ1}),makeQuery(id+"F7.imprint","IMPRINT",EDGE,{"disambiguationData":[TD([[subQ6,1.0]])],"derivedFrom":subQ5}),makeQuery(id+"F7.imprint","IMPRINT",EDGE,{"disambiguationData":[TD([[subQ2,1.0]])],"derivedFrom":subQ0})])],"isStart":true});}
            var sketch = newSketch(context, id + "F19", { "sketchPlane" : qUnion([Q0])});
            skArc(sketch, "E73.0", {"start": v(61.54, -22.6) * mm, "mid": v(76.2, -17.12) * mm, "end": v(90.57, -23.3) * mm});
            skArc(sketch, "E74.0", {"start": v(90.57, -32.23) * mm, "mid": v(76.56, -22.14) * mm, "end": v(61.54, -30.64) * mm});
            skLineSegment(sketch, "E75.0", {"start": v(90.57, -32.23) * mm, "end": v(90.57, -23.3) * mm});
            skLineSegment(sketch, "E76.0", {"start": v(61.54, -30.64) * mm, "end": v(61.54, -22.6) * mm});
            skArc(sketch, "E77.0", {"start": v(90.57, -52.93) * mm, "mid": v(76.2, -59.1) * mm, "end": v(61.54, -53.63) * mm});
            skLineSegment(sketch, "E78.0", {"start": v(61.54, -53.63) * mm, "end": v(61.54, -45.58) * mm});
            skArc(sketch, "E79.0", {"start": v(61.54, -45.58) * mm, "mid": v(76.56, -54.09) * mm, "end": v(90.57, -44) * mm});
            skLineSegment(sketch, "E80.0", {"start": v(90.57, -52.93) * mm, "end": v(90.57, -44) * mm});
            skLineSegment(sketch, "E81", {"start": v(90.57, -32.23) * mm, "end": v(90.57, -44) * mm});
            skLineSegment(sketch, "E82", {"start": v(87.57, -27.4) * mm, "end": v(87.57, -48.83) * mm});
            skLineSegment(sketch, "E83", {"start": v(61.54, -30.64) * mm, "end": v(61.54, -45.58) * mm});
            skLineSegment(sketch, "E84", {"start": v(64.54, -26.64) * mm, "end": v(64.54, -49.59) * mm});
            skSolve(sketch);
        }
        {
            var Q0;
            {var subQ0=sQuery(id+"F19.wireOp",EDGE,"E81");Q0=makeQuery(id+"F19.imprint","IMPRINT",FACE,{"disambiguationData":[TD([[makeQuery(id+"F19.imprint","IMPRINT",EDGE,{"derivedFrom":subQ0}),-1.0]])]});}
            var Q1;
            Q1=makeQuery(id+"F10.opExtrude","SWEPT_BODY",BODY,{"disambiguationData":[OSD([sQuery(id+"F9.wireOp",EDGE,"E60"),sQuery(id+"F9.wireOp",EDGE,"E61")])]});
            extrude(context, id + "F20", {"entities" : qUnion([Q0]), "endBound" : BoundingType.UP_TO_BODY, "oppositeDirection" : true, "endBoundEntityBody" : qUnion([Q1]), "depth" : 25 * mm});
        }
        {
            var Q0;
            {var subQ0=sQuery(id+"F7.wireOp",EDGE,"E57");var subQ1=sQuery(id+"F7.wireOp",EDGE,"E55.0");var subQ6=makeQuery(id+"F7.imprint","INTERSECT",VERTEX,{"disambiguationData":[OD(0.0)],"derivedFrom":[subQ1,subQ0]});var subQ8=makeQuery(id+"F7.imprint","IMPRINT",EDGE,{"disambiguationData":[TD([[subQ6,-1.0]])],"derivedFrom":subQ0});var subQ14=sQuery(id+"F13.wireOp",EDGE,"E62");var subQ15=sQuery(id+"F13.wireOp",EDGE,"E63");Q0=makeQuery(id+"F14.boolean.opBoolean","SPLIT",FACE,{"disambiguationData":[TD([makeQuery(id+"F12.opExtrude","SWEPT_FACE",FACE,{"disambiguationData":[OSD([subQ0]),TDD([subQ8])]})])],"derivedFrom":makeQuery(id+"F14.opExtrude","CAP_FACE",FACE,{"disambiguationData":[OSD([subQ14,subQ15])],"isStart":true})});}
            extrude(context, id + "F21", {"entities" : qUnion([Q0]), "operationType" : NewBodyOperationType.REMOVE, "endBound" : BoundingType.THROUGH_ALL, "oppositeDirection" : true, "depth" : 25 * mm});
        }
        {
            var Q0;
            {var subQ0=sQuery(id+"F19.wireOp",EDGE,"E83");Q0=makeQuery(id+"F19.imprint","IMPRINT",FACE,{"disambiguationData":[TD([[makeQuery(id+"F19.imprint","IMPRINT",EDGE,{"derivedFrom":subQ0}),1.0]])]});}
            extrude(context, id + "F22", {"entities" : qUnion([Q0]), "operationType" : NewBodyOperationType.ADD, "oppositeDirection" : true, "depth" : 7.5 * mm});
        }
        {
            var Q0;
            {var subQ0=sQuery(id+"F15.wireOp",EDGE,"E68");Q0=makeQuery(id+"F15.imprint","IMPRINT",FACE,{"disambiguationData":[TD([[makeQuery(id+"F15.imprint","IMPRINT",EDGE,{"derivedFrom":subQ0}),-1.0]])]});}
            extrude(context, id + "F23", {"entities" : qUnion([Q0]), "oppositeDirection" : true, "depth" : 1 * mm});
        }
    });
